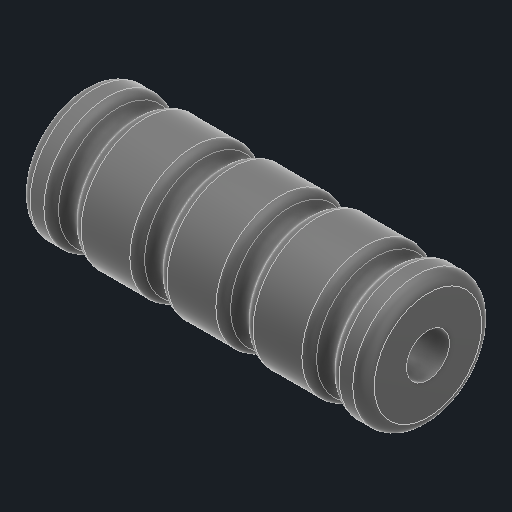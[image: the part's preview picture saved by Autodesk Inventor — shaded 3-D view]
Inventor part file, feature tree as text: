
AUTODESK INVENTOR PART (.ipt)
format: ipt  version: 2025 (Build 290162010, 162A)  size: 244,736 bytes
history: native  units: mm
features: revolve x1, fillet x1, sketch x1
ambient origin geometry x8: Origin, YZ Plane, XZ Plane, XY Plane, X Axis, Y Axis, Z Axis, Center Point
bodies: Solid1 (feature_tree)
feature tree (3):
  revolve  "Revolution1"  [1 undecoded]
  fillet  "Fillet1"  Radius=10.0mm
  sketch  "Sketch1"  dims[d0=80.0mm d1=80.0mm d2=10.0mm d4=5.0mm d5=5.0mm d6=5.0mm d7=5.0mm d9=20.0mm d10=20.0mm d11=10.0mm d12=2.5mm d13=90.0deg d14=10.0mm d15=2.5mm]
note: 1 required parameter value undecoded (feature->parameter linkage not recoverable at this tier; creation-order binding heuristic only, values carry confidence <= 0.55)
